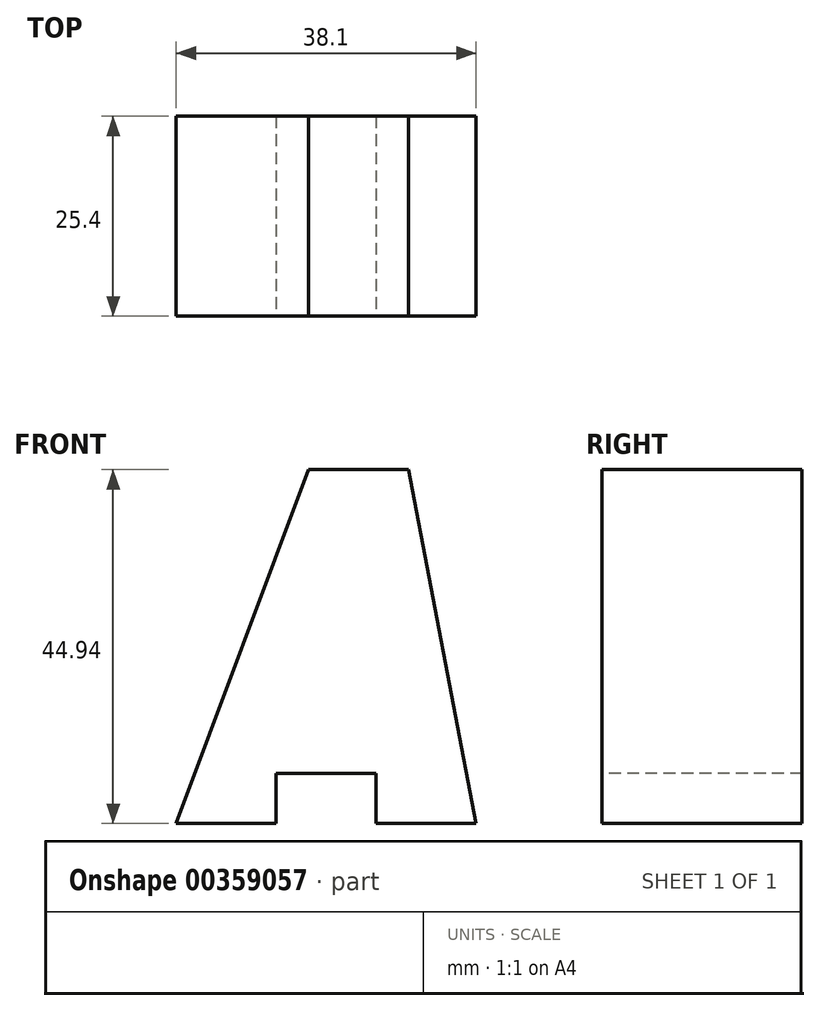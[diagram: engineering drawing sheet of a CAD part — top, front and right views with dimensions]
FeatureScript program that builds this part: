
annotation { "Feature Type Name" : "Feature", "Feature Type Description" : "" }
export const myFeature = defineFeature(function(context is Context, id is Id, definition is map)
    precondition{}
    {
        {
            var Q0;
            Q0=qCreatedBy(makeId("Front.planeOp"),FACE);
            var sketch = newSketch(context, id + "F0", { "sketchPlane" : qUnion([Q0])});
            skLineSegment(sketch, "E0", {"start": v(16.8, 44.94) * mm, "end": v(0, 0) * mm});
            skLineSegment(sketch, "E1", {"start": v(16.8, 44.94) * mm, "end": v(29.5, 44.94) * mm});
            skLineSegment(sketch, "E2", {"start": v(29.5, 44.94) * mm, "end": v(38.1, 0) * mm});
            skLineSegment(sketch, "E3", {"start": v(38.1, 0) * mm, "end": v(25.4, 0) * mm});
            skLineSegment(sketch, "E4", {"start": v(25.4, 0) * mm, "end": v(25.4, 6.35) * mm});
            skLineSegment(sketch, "E5", {"start": v(25.4, 6.35) * mm, "end": v(12.7, 6.35) * mm});
            skLineSegment(sketch, "E6", {"start": v(12.7, 6.35) * mm, "end": v(12.7, 0) * mm});
            skLineSegment(sketch, "E7", {"start": v(12.7, 0) * mm, "end": v(0, 0) * mm});
            skSolve(sketch);
        }
        {
            var Q0;
            Q0=makeQuery(id+"F0.imprint","IMPRINT",FACE,{"disambiguationData":[TD([[makeQuery(id+"F0.imprint","IMPRINT",EDGE,{"derivedFrom":sQuery(id+"F0.wireOp",EDGE,"E0")}),1.0]])]});
            extrude(context, id + "F1", {"entities" : qUnion([Q0]), "oppositeDirection" : true, "depth" : 25.4 * mm});
        }
    });
